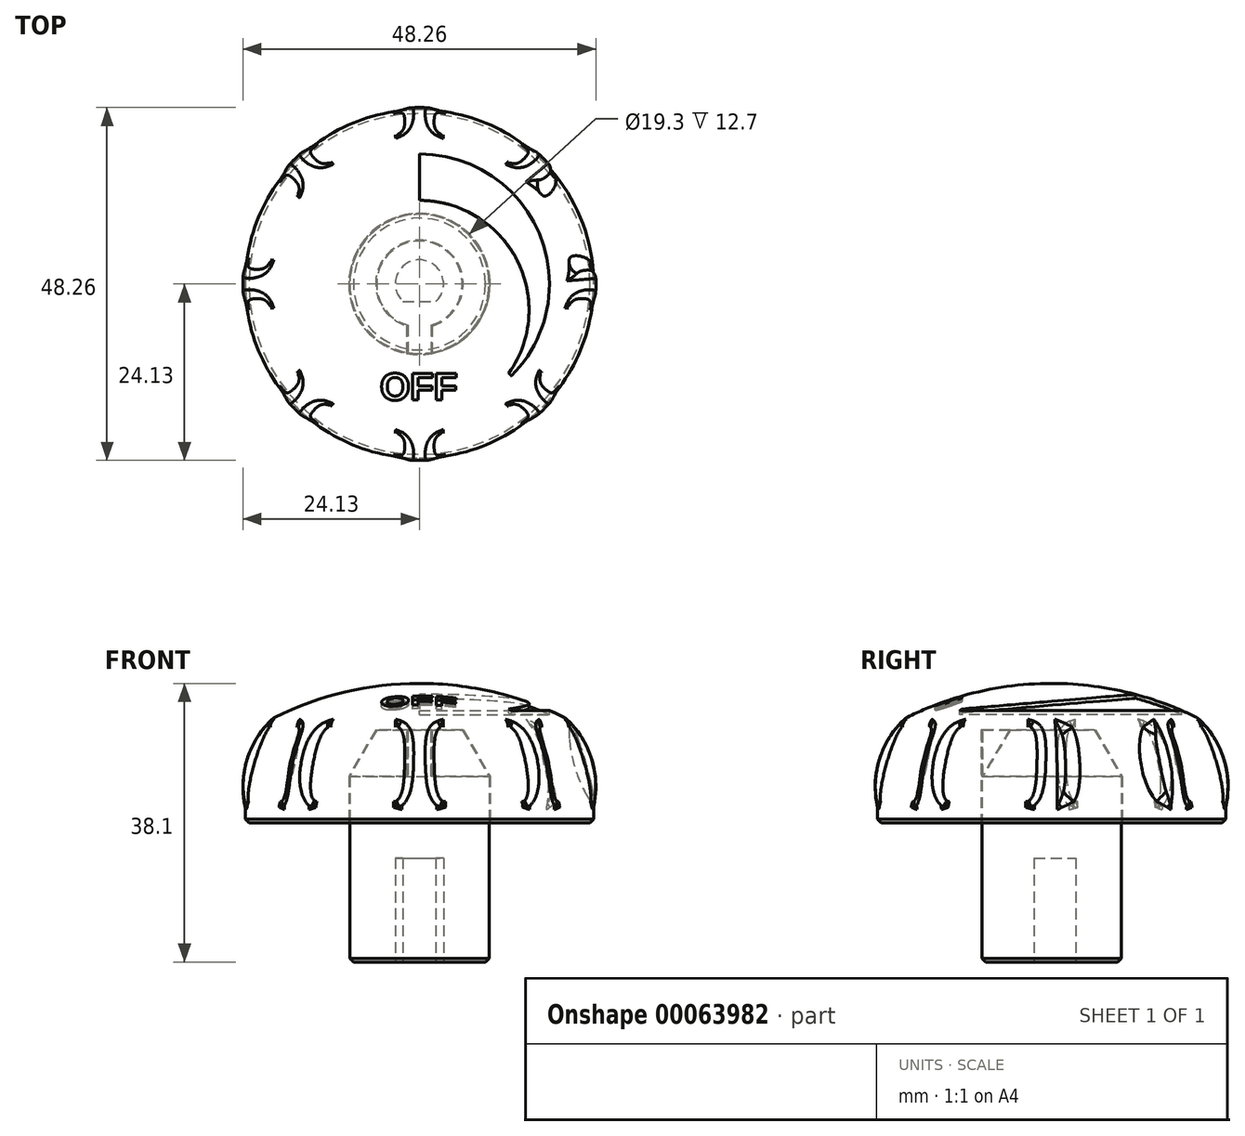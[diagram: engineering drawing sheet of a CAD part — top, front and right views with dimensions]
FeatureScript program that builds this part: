
annotation { "Feature Type Name" : "Feature", "Feature Type Description" : "" }
export const myFeature = defineFeature(function(context is Context, id is Id, definition is map)
    precondition{}
    {
        {
            var Q0;
            Q0=qCreatedBy(makeId("Front.planeOp"),FACE);
            var sketch = newSketch(context, id + "F0", { "sketchPlane" : qUnion([Q0])});
            skLineSegment(sketch, "E0", {"start": v(0, 0) * mm, "end": v(23.81, 0) * mm});
            skLineSegment(sketch, "E1", {"start": v(23.81, 0) * mm, "end": v(23.81, 2.54) * mm});
            skLineSegment(sketch, "E2", {"start": v(0, 0) * mm, "end": v(0, 19.05) * mm});
            skLineSegment(sketch, "E3.MirrorCS", {"start": v(-23.81, 0) * mm, "end": v(-23.81, 2.54) * mm, "construction": true});
            skLineSegment(sketch, "E4.MirrorCS", {"start": v(0, 0) * mm, "end": v(-23.81, 0) * mm, "construction": true});
            skArc(sketch, "E5", {"start": v(20.64, 13.97) * mm, "mid": v(0, 19.05) * mm, "end": v(-20.64, 13.97) * mm});
            skLineSegment(sketch, "E6", {"start": v(20.64, 13.97) * mm, "end": v(20.64, 0) * mm, "construction": true});
            skArc(sketch, "E7", {"start": v(20.64, 13.97) * mm, "mid": v(21.45, 8.04) * mm, "end": v(23.81, 2.54) * mm});
            skSolve(sketch);
        }
        {
            var Q0;
            Q0=makeQuery(id+"F0.imprint","IMPRINT",FACE,{"disambiguationData":[TD([[makeQuery(id+"F0.imprint","IMPRINT",EDGE,{"derivedFrom":sQuery(id+"F0.wireOp",EDGE,"E0")}),1.0]])]});
            var Q1;
            Q1=sQuery(id+"F0.wireOp",EDGE,"E2");
            revolve(context, id + "F1", {"entities" : qUnion([Q0]), "axis" : qUnion([Q1]), "revolveType" : RevolveType.FULL});
        }
        {
            var Q0;
            Q0=makeQuery(id+"F1.opRevolve","SWEPT_EDGE",EDGE,{"disambiguationData":[OSD([sQuery(id+"F0.wireOp",EDGE,"E1"),sQuery(id+"F0.wireOp",EDGE,"E7")])]});
            var Q1;
            Q1=makeQuery(id+"F1.opRevolve","SWEPT_EDGE",EDGE,{"disambiguationData":[OSD([sQuery(id+"F0.wireOp",EDGE,"E5"),sQuery(id+"F0.wireOp",EDGE,"E7")])]});
            fillet(context, id + "F2", {"entities" : qUnion([Q0, Q1]), "radius" : 1.59 * mm, "tangentPropagation" : true, "allowEdgeOverflow" : false});
        }
        {
            var Q0;
            Q0=qCreatedBy(makeId("Front.planeOp"),FACE);
            var sketch = newSketch(context, id + "F3", { "sketchPlane" : qUnion([Q0])});
            skLineSegment(sketch, "E8", {"start": v(0, 0) * mm, "end": v(0, 22.32) * mm, "construction": true});
            skLineSegment(sketch, "E9.0", {"start": v(23.81, 2.1) * mm, "end": v(-23.81, 2.1) * mm, "construction": true});
            skLineSegment(sketch, "E10.0", {"start": v(20.66, 13.05) * mm, "end": v(-20.66, 13.05) * mm, "construction": true});
            skArc(sketch, "E11", {"start": v(20.66, 13.05) * mm, "mid": v(20.4, 13.85) * mm, "end": v(19.78, 14.4) * mm});
            skArc(sketch, "E12", {"start": v(23.81, 2.1) * mm, "mid": v(23.76, 2.52) * mm, "end": v(23.6, 2.9) * mm});
            skArc(sketch, "E13", {"start": v(20.66, 13.05) * mm, "mid": v(21.51, 7.8) * mm, "end": v(23.6, 2.9) * mm});
            skLineSegment(sketch, "E14.0", {"start": v(-19.78, 14.4) * mm, "end": v(19.78, 14.4) * mm, "construction": true});
            skArc(sketch, "E15", {"start": v(23.81, 2.1) * mm, "mid": v(23.58, 8.6) * mm, "end": v(20.16, 14.14) * mm});
            skSolve(sketch);
        }
        {
            var Q0;
            Q0=makeQuery(id+"F3.imprint","IMPRINT",FACE,{"disambiguationData":[TD([[makeQuery(id+"F3.imprint","IMPRINT",EDGE,{"derivedFrom":sQuery(id+"F3.wireOp",EDGE,"E12")}),-1.0]])]});
            var Q1;
            Q1=sQuery(id+"F3.wireOp",EDGE,"E8");
            revolve(context, id + "F4", {"entities" : qUnion([Q0]), "axis" : qUnion([Q1]), "revolveType" : RevolveType.SYMMETRIC, "angle" : 10 * degree});
        }
        {
            var Q0;
            Q0=makeQuery(id+"F4.opRevolve","SWEPT_BODY",BODY,{"disambiguationData":[OSD([sQuery(id+"F3.wireOp",EDGE,"E11"),sQuery(id+"F3.wireOp",EDGE,"E12"),sQuery(id+"F3.wireOp",EDGE,"E13"),sQuery(id+"F3.wireOp",EDGE,"E15")])]});
            var Q1;
            Q1=makeQuery(id+"F1.opRevolve","SWEPT_EDGE",EDGE,{"disambiguationData":[OSD([sQuery(id+"F0.wireOp",EDGE,"E0"),sQuery(id+"F0.wireOp",EDGE,"E1")])]});
            circularPattern(context, id + "F5", {"entities" : qUnion([Q0]), "axis" : qUnion([Q1]), "angle" : 360 * degree, "instanceCount" : 8, "equalSpace" : true});
        }
        {
            var Q0;
            Q0=makeQuery(id+"F5.opPattern","COPY",BODY,{"derivedFrom":makeQuery(id+"F4.opRevolve","SWEPT_BODY",BODY,{"disambiguationData":[OSD([sQuery(id+"F3.wireOp",EDGE,"E11"),sQuery(id+"F3.wireOp",EDGE,"E12"),sQuery(id+"F3.wireOp",EDGE,"E13"),sQuery(id+"F3.wireOp",EDGE,"E15")])]}),"instanceName":"4"});
            var Q1;
            Q1=makeQuery(id+"F1.opRevolve","SWEPT_BODY",BODY,{"disambiguationData":[OSD([sQuery(id+"F0.wireOp",EDGE,"E0"),sQuery(id+"F0.wireOp",EDGE,"E1"),sQuery(id+"F0.wireOp",EDGE,"E2"),sQuery(id+"F0.wireOp",EDGE,"E5"),sQuery(id+"F0.wireOp",EDGE,"E7")])]});
            var Q2;
            Q2=makeQuery(id+"F5.opPattern","COPY",BODY,{"derivedFrom":makeQuery(id+"F4.opRevolve","SWEPT_BODY",BODY,{"disambiguationData":[OSD([sQuery(id+"F3.wireOp",EDGE,"E11"),sQuery(id+"F3.wireOp",EDGE,"E12"),sQuery(id+"F3.wireOp",EDGE,"E13"),sQuery(id+"F3.wireOp",EDGE,"E15")])]}),"instanceName":"7"});
            var Q3;
            Q3=makeQuery(id+"F5.opPattern","COPY",BODY,{"derivedFrom":makeQuery(id+"F4.opRevolve","SWEPT_BODY",BODY,{"disambiguationData":[OSD([sQuery(id+"F3.wireOp",EDGE,"E11"),sQuery(id+"F3.wireOp",EDGE,"E12"),sQuery(id+"F3.wireOp",EDGE,"E13"),sQuery(id+"F3.wireOp",EDGE,"E15")])]}),"instanceName":"6"});
            var Q4;
            Q4=makeQuery(id+"F5.opPattern","COPY",BODY,{"derivedFrom":makeQuery(id+"F4.opRevolve","SWEPT_BODY",BODY,{"disambiguationData":[OSD([sQuery(id+"F3.wireOp",EDGE,"E11"),sQuery(id+"F3.wireOp",EDGE,"E12"),sQuery(id+"F3.wireOp",EDGE,"E13"),sQuery(id+"F3.wireOp",EDGE,"E15")])]}),"instanceName":"5"});
            var Q5;
            Q5=makeQuery(id+"F4.opRevolve","SWEPT_BODY",BODY,{"disambiguationData":[OSD([sQuery(id+"F3.wireOp",EDGE,"E11"),sQuery(id+"F3.wireOp",EDGE,"E12"),sQuery(id+"F3.wireOp",EDGE,"E13"),sQuery(id+"F3.wireOp",EDGE,"E15")])]});
            var Q6;
            Q6=makeQuery(id+"F5.opPattern","COPY",BODY,{"derivedFrom":makeQuery(id+"F4.opRevolve","SWEPT_BODY",BODY,{"disambiguationData":[OSD([sQuery(id+"F3.wireOp",EDGE,"E11"),sQuery(id+"F3.wireOp",EDGE,"E12"),sQuery(id+"F3.wireOp",EDGE,"E13"),sQuery(id+"F3.wireOp",EDGE,"E15")])]}),"instanceName":"1"});
            var Q7;
            Q7=makeQuery(id+"F5.opPattern","COPY",BODY,{"derivedFrom":makeQuery(id+"F4.opRevolve","SWEPT_BODY",BODY,{"disambiguationData":[OSD([sQuery(id+"F3.wireOp",EDGE,"E11"),sQuery(id+"F3.wireOp",EDGE,"E12"),sQuery(id+"F3.wireOp",EDGE,"E13"),sQuery(id+"F3.wireOp",EDGE,"E15")])]}),"instanceName":"2"});
            var Q8;
            Q8=makeQuery(id+"F5.opPattern","COPY",BODY,{"derivedFrom":makeQuery(id+"F4.opRevolve","SWEPT_BODY",BODY,{"disambiguationData":[OSD([sQuery(id+"F3.wireOp",EDGE,"E11"),sQuery(id+"F3.wireOp",EDGE,"E12"),sQuery(id+"F3.wireOp",EDGE,"E13"),sQuery(id+"F3.wireOp",EDGE,"E15")])]}),"instanceName":"3"});
            booleanBodies(context, id + "F6", {"operationType" : BooleanOperationType.UNION, "tools" : qUnion([Q0, Q1, Q2, Q3, Q4, Q5, Q6, Q7, Q8])});
        }
        {
            var Q0;
            Q0=makeQuery(id+"F5.opPattern","COPY",EDGE,{"derivedFrom":makeQuery(id+"F4.opRevolve","CAP_EDGE",EDGE,{"disambiguationData":[OSD([sQuery(id+"F3.wireOp",EDGE,"E13")])],"isStart":false}),"instanceName":"4"});
            var Q1;
            Q1=makeQuery(id+"F5.opPattern","COPY",EDGE,{"derivedFrom":makeQuery(id+"F4.opRevolve","CAP_EDGE",EDGE,{"disambiguationData":[OSD([sQuery(id+"F3.wireOp",EDGE,"E13")])],"isStart":true}),"instanceName":"4"});
            var Q2;
            Q2=makeQuery(id+"F5.opPattern","COPY",EDGE,{"derivedFrom":makeQuery(id+"F4.opRevolve","CAP_EDGE",EDGE,{"disambiguationData":[OSD([sQuery(id+"F3.wireOp",EDGE,"E13")])],"isStart":false}),"instanceName":"5"});
            var Q3;
            Q3=makeQuery(id+"F5.opPattern","COPY",EDGE,{"derivedFrom":makeQuery(id+"F4.opRevolve","CAP_EDGE",EDGE,{"disambiguationData":[OSD([sQuery(id+"F3.wireOp",EDGE,"E13")])],"isStart":true}),"instanceName":"5"});
            var Q4;
            Q4=makeQuery(id+"F5.opPattern","COPY",EDGE,{"derivedFrom":makeQuery(id+"F4.opRevolve","CAP_EDGE",EDGE,{"disambiguationData":[OSD([sQuery(id+"F3.wireOp",EDGE,"E13")])],"isStart":false}),"instanceName":"6"});
            var Q5;
            Q5=makeQuery(id+"F5.opPattern","COPY",EDGE,{"derivedFrom":makeQuery(id+"F4.opRevolve","CAP_EDGE",EDGE,{"disambiguationData":[OSD([sQuery(id+"F3.wireOp",EDGE,"E13")])],"isStart":true}),"instanceName":"6"});
            var Q6;
            Q6=makeQuery(id+"F5.opPattern","COPY",EDGE,{"derivedFrom":makeQuery(id+"F4.opRevolve","CAP_EDGE",EDGE,{"disambiguationData":[OSD([sQuery(id+"F3.wireOp",EDGE,"E13")])],"isStart":false}),"instanceName":"7"});
            var Q7;
            Q7=makeQuery(id+"F5.opPattern","COPY",EDGE,{"derivedFrom":makeQuery(id+"F4.opRevolve","CAP_EDGE",EDGE,{"disambiguationData":[OSD([sQuery(id+"F3.wireOp",EDGE,"E13")])],"isStart":true}),"instanceName":"7"});
            var Q8;
            Q8=makeQuery(id+"F4.opRevolve","CAP_EDGE",EDGE,{"disambiguationData":[OSD([sQuery(id+"F3.wireOp",EDGE,"E13")])],"isStart":false});
            var Q9;
            Q9=makeQuery(id+"F4.opRevolve","CAP_EDGE",EDGE,{"disambiguationData":[OSD([sQuery(id+"F3.wireOp",EDGE,"E13")])],"isStart":true});
            var Q10;
            Q10=makeQuery(id+"F5.opPattern","COPY",EDGE,{"derivedFrom":makeQuery(id+"F4.opRevolve","CAP_EDGE",EDGE,{"disambiguationData":[OSD([sQuery(id+"F3.wireOp",EDGE,"E13")])],"isStart":false}),"instanceName":"1"});
            var Q11;
            Q11=makeQuery(id+"F5.opPattern","COPY",EDGE,{"derivedFrom":makeQuery(id+"F4.opRevolve","CAP_EDGE",EDGE,{"disambiguationData":[OSD([sQuery(id+"F3.wireOp",EDGE,"E13")])],"isStart":true}),"instanceName":"1"});
            var Q12;
            Q12=makeQuery(id+"F5.opPattern","COPY",EDGE,{"derivedFrom":makeQuery(id+"F4.opRevolve","CAP_EDGE",EDGE,{"disambiguationData":[OSD([sQuery(id+"F3.wireOp",EDGE,"E13")])],"isStart":false}),"instanceName":"2"});
            var Q13;
            Q13=makeQuery(id+"F5.opPattern","COPY",EDGE,{"derivedFrom":makeQuery(id+"F4.opRevolve","CAP_EDGE",EDGE,{"disambiguationData":[OSD([sQuery(id+"F3.wireOp",EDGE,"E13")])],"isStart":true}),"instanceName":"2"});
            var Q14;
            Q14=makeQuery(id+"F5.opPattern","COPY",EDGE,{"derivedFrom":makeQuery(id+"F4.opRevolve","CAP_EDGE",EDGE,{"disambiguationData":[OSD([sQuery(id+"F3.wireOp",EDGE,"E13")])],"isStart":false}),"instanceName":"3"});
            var Q15;
            Q15=makeQuery(id+"F5.opPattern","COPY",EDGE,{"derivedFrom":makeQuery(id+"F4.opRevolve","CAP_EDGE",EDGE,{"disambiguationData":[OSD([sQuery(id+"F3.wireOp",EDGE,"E13")])],"isStart":true}),"instanceName":"3"});
            fillet(context, id + "F7", {"entities" : qUnion([Q0, Q1, Q2, Q3, Q4, Q5, Q6, Q7, Q8, Q9, Q10, Q11, Q12, Q13, Q14, Q15]), "radius" : 1.59 * mm, "tangentPropagation" : true, "allowEdgeOverflow" : false});
        }
        {
            var Q0;
            Q0=makeQuery(id+"F5.opPattern","COPY",EDGE,{"derivedFrom":makeQuery(id+"F4.opRevolve","CAP_EDGE",EDGE,{"disambiguationData":[OSD([sQuery(id+"F3.wireOp",EDGE,"E15")])],"isStart":false}),"instanceName":"5"});
            var Q1;
            Q1=makeQuery(id+"F5.opPattern","COPY",EDGE,{"derivedFrom":makeQuery(id+"F4.opRevolve","CAP_EDGE",EDGE,{"disambiguationData":[OSD([sQuery(id+"F3.wireOp",EDGE,"E15")])],"isStart":true}),"instanceName":"5"});
            var Q2;
            Q2=makeQuery(id+"F5.opPattern","COPY",EDGE,{"derivedFrom":makeQuery(id+"F4.opRevolve","CAP_EDGE",EDGE,{"disambiguationData":[OSD([sQuery(id+"F3.wireOp",EDGE,"E15")])],"isStart":false}),"instanceName":"6"});
            var Q3;
            Q3=makeQuery(id+"F5.opPattern","COPY",EDGE,{"derivedFrom":makeQuery(id+"F4.opRevolve","CAP_EDGE",EDGE,{"disambiguationData":[OSD([sQuery(id+"F3.wireOp",EDGE,"E15")])],"isStart":true}),"instanceName":"6"});
            var Q4;
            Q4=makeQuery(id+"F5.opPattern","COPY",EDGE,{"derivedFrom":makeQuery(id+"F4.opRevolve","CAP_EDGE",EDGE,{"disambiguationData":[OSD([sQuery(id+"F3.wireOp",EDGE,"E15")])],"isStart":false}),"instanceName":"7"});
            var Q5;
            Q5=makeQuery(id+"F5.opPattern","COPY",EDGE,{"derivedFrom":makeQuery(id+"F4.opRevolve","CAP_EDGE",EDGE,{"disambiguationData":[OSD([sQuery(id+"F3.wireOp",EDGE,"E15")])],"isStart":true}),"instanceName":"7"});
            var Q6;
            Q6=makeQuery(id+"F4.opRevolve","CAP_EDGE",EDGE,{"disambiguationData":[OSD([sQuery(id+"F3.wireOp",EDGE,"E15")])],"isStart":false});
            var Q7;
            Q7=makeQuery(id+"F4.opRevolve","CAP_EDGE",EDGE,{"disambiguationData":[OSD([sQuery(id+"F3.wireOp",EDGE,"E15")])],"isStart":true});
            var Q8;
            Q8=makeQuery(id+"F5.opPattern","COPY",EDGE,{"derivedFrom":makeQuery(id+"F4.opRevolve","CAP_EDGE",EDGE,{"disambiguationData":[OSD([sQuery(id+"F3.wireOp",EDGE,"E15")])],"isStart":false}),"instanceName":"1"});
            var Q9;
            Q9=makeQuery(id+"F5.opPattern","COPY",EDGE,{"derivedFrom":makeQuery(id+"F4.opRevolve","CAP_EDGE",EDGE,{"disambiguationData":[OSD([sQuery(id+"F3.wireOp",EDGE,"E15")])],"isStart":true}),"instanceName":"1"});
            var Q10;
            Q10=makeQuery(id+"F5.opPattern","COPY",EDGE,{"derivedFrom":makeQuery(id+"F4.opRevolve","CAP_EDGE",EDGE,{"disambiguationData":[OSD([sQuery(id+"F3.wireOp",EDGE,"E15")])],"isStart":false}),"instanceName":"2"});
            var Q11;
            Q11=makeQuery(id+"F5.opPattern","COPY",EDGE,{"derivedFrom":makeQuery(id+"F4.opRevolve","CAP_EDGE",EDGE,{"disambiguationData":[OSD([sQuery(id+"F3.wireOp",EDGE,"E15")])],"isStart":true}),"instanceName":"2"});
            var Q12;
            Q12=makeQuery(id+"F5.opPattern","COPY",EDGE,{"derivedFrom":makeQuery(id+"F4.opRevolve","CAP_EDGE",EDGE,{"disambiguationData":[OSD([sQuery(id+"F3.wireOp",EDGE,"E15")])],"isStart":false}),"instanceName":"3"});
            var Q13;
            Q13=makeQuery(id+"F5.opPattern","COPY",EDGE,{"derivedFrom":makeQuery(id+"F4.opRevolve","CAP_EDGE",EDGE,{"disambiguationData":[OSD([sQuery(id+"F3.wireOp",EDGE,"E15")])],"isStart":true}),"instanceName":"3"});
            var Q14;
            Q14=makeQuery(id+"F5.opPattern","COPY",EDGE,{"derivedFrom":makeQuery(id+"F4.opRevolve","CAP_EDGE",EDGE,{"disambiguationData":[OSD([sQuery(id+"F3.wireOp",EDGE,"E15")])],"isStart":false}),"instanceName":"4"});
            var Q15;
            Q15=makeQuery(id+"F5.opPattern","COPY",EDGE,{"derivedFrom":makeQuery(id+"F4.opRevolve","CAP_EDGE",EDGE,{"disambiguationData":[OSD([sQuery(id+"F3.wireOp",EDGE,"E15")])],"isStart":true}),"instanceName":"4"});
            fillet(context, id + "F8", {"entities" : qUnion([Q0, Q1, Q2, Q3, Q4, Q5, Q6, Q7, Q8, Q9, Q10, Q11, Q12, Q13, Q14, Q15]), "radius" : 1.27 * mm, "tangentPropagation" : true, "allowEdgeOverflow" : false});
        }
        {
            var Q0;
            {var subQ0=sQuery(id+"F3.wireOp",EDGE,"E15");var subQ3=sQuery(id+"F3.wireOp",EDGE,"E13");var subQ4=sQuery(id+"F3.wireOp",EDGE,"E12");var subQ5=sQuery(id+"F3.wireOp",EDGE,"E11");var subQ6=makeQuery(id+"F4.opRevolve","CAP_FACE",FACE,{"disambiguationData":[OSD([subQ5,subQ4,subQ3,subQ0])],"isStart":true});var subQ7=sQuery(id+"F0.wireOp",EDGE,"E7");var subQ8=sQuery(id+"F0.wireOp",EDGE,"E1");var subQ10=makeQuery(id+"F1.opRevolve","SWEPT_FACE",FACE,{"disambiguationData":[OSD([subQ8])]});var subQ12=makeQuery(id+"F2.opFillet","BLEND_EDGE",EDGE,{"blendedFrom":[makeQuery(id+"F1.opRevolve","SWEPT_EDGE",EDGE,{"disambiguationData":[OSD([subQ8,subQ7])]}),subQ10],"blendedInto":[subQ10]});Q0=makeQuery(id+"F7.opFillet","MERGE",EDGE,{"derivedFrom":[makeQuery(id+"F6.opBoolean","MERGE",EDGE,{"derivedFrom":[subQ12,makeQuery(id+"F5.opPattern","COPY",EDGE,{"derivedFrom":makeQuery(id+"F4.opRevolve","SWEPT_EDGE",EDGE,{"disambiguationData":[OSD([subQ4,subQ0])]}),"instanceName":"6"})]}),makeQuery(id+"F6.opBoolean","SPLIT",EDGE,{"disambiguationData":[TD([makeQuery(id+"F5.opPattern","COPY",FACE,{"derivedFrom":subQ6,"instanceName":"5"})])],"derivedFrom":subQ12}),makeQuery(id+"F6.opBoolean","SPLIT",EDGE,{"disambiguationData":[TD([makeQuery(id+"F5.opPattern","COPY",FACE,{"derivedFrom":subQ6,"instanceName":"6"})])],"derivedFrom":subQ12})]});}
            var Q1;
            {var subQ0=sQuery(id+"F3.wireOp",EDGE,"E15");var subQ3=sQuery(id+"F3.wireOp",EDGE,"E13");var subQ4=sQuery(id+"F3.wireOp",EDGE,"E12");var subQ5=sQuery(id+"F3.wireOp",EDGE,"E11");var subQ6=makeQuery(id+"F4.opRevolve","CAP_FACE",FACE,{"disambiguationData":[OSD([subQ5,subQ4,subQ3,subQ0])],"isStart":true});var subQ7=sQuery(id+"F0.wireOp",EDGE,"E1");var subQ8=makeQuery(id+"F1.opRevolve","SWEPT_FACE",FACE,{"disambiguationData":[OSD([subQ7])]});var subQ9=sQuery(id+"F0.wireOp",EDGE,"E7");var subQ12=makeQuery(id+"F2.opFillet","BLEND_EDGE",EDGE,{"blendedFrom":[makeQuery(id+"F1.opRevolve","SWEPT_EDGE",EDGE,{"disambiguationData":[OSD([subQ7,subQ9])]}),subQ8],"blendedInto":[subQ8]});Q1=makeQuery(id+"F7.opFillet","MERGE",EDGE,{"derivedFrom":[makeQuery(id+"F6.opBoolean","MERGE",EDGE,{"derivedFrom":[subQ12,makeQuery(id+"F5.opPattern","COPY",EDGE,{"derivedFrom":makeQuery(id+"F4.opRevolve","SWEPT_EDGE",EDGE,{"disambiguationData":[OSD([subQ4,subQ0])]}),"instanceName":"5"})]}),makeQuery(id+"F6.opBoolean","SPLIT",EDGE,{"disambiguationData":[TD([makeQuery(id+"F5.opPattern","COPY",FACE,{"derivedFrom":subQ6,"instanceName":"4"})])],"derivedFrom":subQ12}),makeQuery(id+"F6.opBoolean","SPLIT",EDGE,{"disambiguationData":[TD([makeQuery(id+"F5.opPattern","COPY",FACE,{"derivedFrom":subQ6,"instanceName":"5"})])],"derivedFrom":subQ12})]});}
            var Q2;
            {var subQ0=sQuery(id+"F3.wireOp",EDGE,"E15");var subQ3=sQuery(id+"F3.wireOp",EDGE,"E13");var subQ4=sQuery(id+"F3.wireOp",EDGE,"E12");var subQ5=sQuery(id+"F3.wireOp",EDGE,"E11");var subQ6=makeQuery(id+"F4.opRevolve","CAP_FACE",FACE,{"disambiguationData":[OSD([subQ5,subQ4,subQ3,subQ0])],"isStart":true});var subQ7=sQuery(id+"F0.wireOp",EDGE,"E7");var subQ8=sQuery(id+"F0.wireOp",EDGE,"E1");var subQ10=makeQuery(id+"F1.opRevolve","SWEPT_FACE",FACE,{"disambiguationData":[OSD([subQ8])]});var subQ12=makeQuery(id+"F2.opFillet","BLEND_EDGE",EDGE,{"blendedFrom":[makeQuery(id+"F1.opRevolve","SWEPT_EDGE",EDGE,{"disambiguationData":[OSD([subQ8,subQ7])]}),subQ10],"blendedInto":[subQ10]});Q2=makeQuery(id+"F7.opFillet","MERGE",EDGE,{"derivedFrom":[makeQuery(id+"F6.opBoolean","MERGE",EDGE,{"derivedFrom":[subQ12,makeQuery(id+"F5.opPattern","COPY",EDGE,{"derivedFrom":makeQuery(id+"F4.opRevolve","SWEPT_EDGE",EDGE,{"disambiguationData":[OSD([subQ4,subQ0])]}),"instanceName":"4"})]}),makeQuery(id+"F6.opBoolean","SPLIT",EDGE,{"disambiguationData":[TD([makeQuery(id+"F5.opPattern","COPY",FACE,{"derivedFrom":subQ6,"instanceName":"3"})])],"derivedFrom":subQ12}),makeQuery(id+"F6.opBoolean","SPLIT",EDGE,{"disambiguationData":[TD([makeQuery(id+"F5.opPattern","COPY",FACE,{"derivedFrom":subQ6,"instanceName":"4"})])],"derivedFrom":subQ12})]});}
            var Q3;
            {var subQ0=sQuery(id+"F3.wireOp",EDGE,"E15");var subQ3=sQuery(id+"F0.wireOp",EDGE,"E7");var subQ4=sQuery(id+"F0.wireOp",EDGE,"E1");var subQ6=sQuery(id+"F3.wireOp",EDGE,"E13");var subQ7=sQuery(id+"F3.wireOp",EDGE,"E12");var subQ8=sQuery(id+"F3.wireOp",EDGE,"E11");var subQ9=makeQuery(id+"F4.opRevolve","CAP_FACE",FACE,{"disambiguationData":[OSD([subQ8,subQ7,subQ6,subQ0])],"isStart":true});var subQ10=makeQuery(id+"F1.opRevolve","SWEPT_FACE",FACE,{"disambiguationData":[OSD([subQ4])]});var subQ12=makeQuery(id+"F2.opFillet","BLEND_EDGE",EDGE,{"blendedFrom":[makeQuery(id+"F1.opRevolve","SWEPT_EDGE",EDGE,{"disambiguationData":[OSD([subQ4,subQ3])]}),subQ10],"blendedInto":[subQ10]});Q3=makeQuery(id+"F7.opFillet","MERGE",EDGE,{"derivedFrom":[makeQuery(id+"F6.opBoolean","MERGE",EDGE,{"derivedFrom":[subQ12,makeQuery(id+"F5.opPattern","COPY",EDGE,{"derivedFrom":makeQuery(id+"F4.opRevolve","SWEPT_EDGE",EDGE,{"disambiguationData":[OSD([subQ7,subQ0])]}),"instanceName":"3"})]}),makeQuery(id+"F6.opBoolean","SPLIT",EDGE,{"disambiguationData":[TD([makeQuery(id+"F5.opPattern","COPY",FACE,{"derivedFrom":subQ9,"instanceName":"2"})])],"derivedFrom":subQ12}),makeQuery(id+"F6.opBoolean","SPLIT",EDGE,{"disambiguationData":[TD([makeQuery(id+"F5.opPattern","COPY",FACE,{"derivedFrom":subQ9,"instanceName":"3"})])],"derivedFrom":subQ12})]});}
            var Q4;
            {var subQ0=sQuery(id+"F3.wireOp",EDGE,"E15");var subQ1=sQuery(id+"F3.wireOp",EDGE,"E13");var subQ2=sQuery(id+"F3.wireOp",EDGE,"E12");var subQ3=sQuery(id+"F3.wireOp",EDGE,"E11");var subQ4=makeQuery(id+"F4.opRevolve","CAP_FACE",FACE,{"disambiguationData":[OSD([subQ3,subQ2,subQ1,subQ0])],"isStart":true});var subQ7=sQuery(id+"F0.wireOp",EDGE,"E7");var subQ8=sQuery(id+"F0.wireOp",EDGE,"E1");var subQ10=makeQuery(id+"F1.opRevolve","SWEPT_FACE",FACE,{"disambiguationData":[OSD([subQ8])]});var subQ12=makeQuery(id+"F2.opFillet","BLEND_EDGE",EDGE,{"blendedFrom":[makeQuery(id+"F1.opRevolve","SWEPT_EDGE",EDGE,{"disambiguationData":[OSD([subQ8,subQ7])]}),subQ10],"blendedInto":[subQ10]});Q4=makeQuery(id+"F7.opFillet","MERGE",EDGE,{"derivedFrom":[makeQuery(id+"F6.opBoolean","MERGE",EDGE,{"derivedFrom":[subQ12,makeQuery(id+"F5.opPattern","COPY",EDGE,{"derivedFrom":makeQuery(id+"F4.opRevolve","SWEPT_EDGE",EDGE,{"disambiguationData":[OSD([subQ2,subQ0])]}),"instanceName":"2"})]}),makeQuery(id+"F6.opBoolean","SPLIT",EDGE,{"disambiguationData":[TD([makeQuery(id+"F5.opPattern","COPY",FACE,{"derivedFrom":subQ4,"instanceName":"1"})])],"derivedFrom":subQ12}),makeQuery(id+"F6.opBoolean","SPLIT",EDGE,{"disambiguationData":[TD([makeQuery(id+"F5.opPattern","COPY",FACE,{"derivedFrom":subQ4,"instanceName":"2"})])],"derivedFrom":subQ12})]});}
            var Q5;
            {var subQ0=sQuery(id+"F3.wireOp",EDGE,"E15");var subQ3=sQuery(id+"F3.wireOp",EDGE,"E13");var subQ4=sQuery(id+"F3.wireOp",EDGE,"E12");var subQ5=sQuery(id+"F3.wireOp",EDGE,"E11");var subQ6=makeQuery(id+"F4.opRevolve","CAP_FACE",FACE,{"disambiguationData":[OSD([subQ5,subQ4,subQ3,subQ0])],"isStart":true});var subQ7=sQuery(id+"F0.wireOp",EDGE,"E7");var subQ8=sQuery(id+"F0.wireOp",EDGE,"E1");var subQ10=makeQuery(id+"F1.opRevolve","SWEPT_FACE",FACE,{"disambiguationData":[OSD([subQ8])]});var subQ12=makeQuery(id+"F2.opFillet","BLEND_EDGE",EDGE,{"blendedFrom":[makeQuery(id+"F1.opRevolve","SWEPT_EDGE",EDGE,{"disambiguationData":[OSD([subQ8,subQ7])]}),subQ10],"blendedInto":[subQ10]});Q5=makeQuery(id+"F7.opFillet","MERGE",EDGE,{"derivedFrom":[makeQuery(id+"F6.opBoolean","MERGE",EDGE,{"derivedFrom":[subQ12,makeQuery(id+"F5.opPattern","COPY",EDGE,{"derivedFrom":makeQuery(id+"F4.opRevolve","SWEPT_EDGE",EDGE,{"disambiguationData":[OSD([subQ4,subQ0])]}),"instanceName":"1"})]}),makeQuery(id+"F6.opBoolean","SPLIT",EDGE,{"disambiguationData":[TD([subQ6])],"derivedFrom":subQ12}),makeQuery(id+"F6.opBoolean","SPLIT",EDGE,{"disambiguationData":[TD([makeQuery(id+"F5.opPattern","COPY",FACE,{"derivedFrom":subQ6,"instanceName":"1"})])],"derivedFrom":subQ12})]});}
            var Q6;
            {var subQ0=sQuery(id+"F3.wireOp",EDGE,"E15");var subQ2=sQuery(id+"F3.wireOp",EDGE,"E13");var subQ3=sQuery(id+"F3.wireOp",EDGE,"E12");var subQ4=sQuery(id+"F3.wireOp",EDGE,"E11");var subQ5=makeQuery(id+"F4.opRevolve","CAP_FACE",FACE,{"disambiguationData":[OSD([subQ4,subQ3,subQ2,subQ0])],"isStart":false});var subQ6=sQuery(id+"F0.wireOp",EDGE,"E7");var subQ7=sQuery(id+"F0.wireOp",EDGE,"E1");var subQ9=makeQuery(id+"F1.opRevolve","SWEPT_FACE",FACE,{"disambiguationData":[OSD([subQ7])]});var subQ10=makeQuery(id+"F4.opRevolve","CAP_FACE",FACE,{"disambiguationData":[OSD([subQ4,subQ3,subQ2,subQ0])],"isStart":true});var subQ11=makeQuery(id+"F2.opFillet","BLEND_EDGE",EDGE,{"blendedFrom":[makeQuery(id+"F1.opRevolve","SWEPT_EDGE",EDGE,{"disambiguationData":[OSD([subQ7,subQ6])]}),subQ9],"blendedInto":[subQ9]});Q6=makeQuery(id+"F7.opFillet","MERGE",EDGE,{"derivedFrom":[makeQuery(id+"F6.opBoolean","MERGE",EDGE,{"derivedFrom":[subQ11,makeQuery(id+"F4.opRevolve","SWEPT_EDGE",EDGE,{"disambiguationData":[OSD([subQ3,subQ0])]})]}),makeQuery(id+"F6.opBoolean","SPLIT",EDGE,{"disambiguationData":[TD([subQ10])],"derivedFrom":subQ11}),makeQuery(id+"F6.opBoolean","SPLIT",EDGE,{"disambiguationData":[TD([subQ5])],"derivedFrom":subQ11})]});}
            var Q7;
            {var subQ0=sQuery(id+"F3.wireOp",EDGE,"E15");var subQ2=sQuery(id+"F3.wireOp",EDGE,"E13");var subQ3=sQuery(id+"F3.wireOp",EDGE,"E12");var subQ4=sQuery(id+"F3.wireOp",EDGE,"E11");var subQ5=makeQuery(id+"F4.opRevolve","CAP_FACE",FACE,{"disambiguationData":[OSD([subQ4,subQ3,subQ2,subQ0])],"isStart":true});var subQ6=sQuery(id+"F0.wireOp",EDGE,"E7");var subQ7=sQuery(id+"F0.wireOp",EDGE,"E1");var subQ9=makeQuery(id+"F1.opRevolve","SWEPT_FACE",FACE,{"disambiguationData":[OSD([subQ7])]});var subQ10=makeQuery(id+"F4.opRevolve","CAP_FACE",FACE,{"disambiguationData":[OSD([subQ4,subQ3,subQ2,subQ0])],"isStart":false});var subQ12=makeQuery(id+"F2.opFillet","BLEND_EDGE",EDGE,{"blendedFrom":[makeQuery(id+"F1.opRevolve","SWEPT_EDGE",EDGE,{"disambiguationData":[OSD([subQ7,subQ6])]}),subQ9],"blendedInto":[subQ9]});Q7=makeQuery(id+"F7.opFillet","MERGE",EDGE,{"derivedFrom":[makeQuery(id+"F6.opBoolean","MERGE",EDGE,{"derivedFrom":[subQ12,makeQuery(id+"F5.opPattern","COPY",EDGE,{"derivedFrom":makeQuery(id+"F4.opRevolve","SWEPT_EDGE",EDGE,{"disambiguationData":[OSD([subQ3,subQ0])]}),"instanceName":"7"})]}),makeQuery(id+"F6.opBoolean","SPLIT",EDGE,{"disambiguationData":[TD([subQ10])],"derivedFrom":subQ12}),makeQuery(id+"F6.opBoolean","SPLIT",EDGE,{"disambiguationData":[TD([makeQuery(id+"F5.opPattern","COPY",FACE,{"derivedFrom":subQ5,"instanceName":"6"})])],"derivedFrom":subQ12})]});}
            fillet(context, id + "F9", {"entities" : qUnion([Q0, Q1, Q2, Q3, Q4, Q5, Q6, Q7]), "radius" : 2.54 * mm, "tangentPropagation" : true, "allowEdgeOverflow" : false});
        }
        {
            var Q0;
            Q0=qCreatedBy(makeId("Front.planeOp"),FACE);
            var sketch = newSketch(context, id + "F10", { "sketchPlane" : qUnion([Q0])});
            skLineSegment(sketch, "E16.0.0", {"start": v(23.55, 0) * mm, "end": v(-22.88, 0) * mm, "construction": true});
            skArc(sketch, "E17", {"start": v(19.78, 14.4) * mm, "mid": v(0, 19.05) * mm, "end": v(-19.78, 14.4) * mm, "construction": true});
            skLineSegment(sketch, "E18", {"start": v(0, 0) * mm, "end": v(0, 19.05) * mm, "construction": true});
            skLineSegment(sketch, "E19", {"start": v(0, 0) * mm, "end": v(0, -25.4) * mm, "construction": true});
            skLineSegment(sketch, "E20", {"start": v(0, 12.7) * mm, "end": v(5.99, 12.7) * mm});
            skLineSegment(sketch, "E21", {"start": v(5.99, 12.7) * mm, "end": v(9.65, 6.35) * mm});
            skLineSegment(sketch, "E22", {"start": v(9.65, 6.35) * mm, "end": v(9.65, 0) * mm});
            skLineSegment(sketch, "E23", {"start": v(9.65, 0) * mm, "end": v(0, 0) * mm});
            skLineSegment(sketch, "E24", {"start": v(0, 12.7) * mm, "end": v(0, 0) * mm});
            skSolve(sketch);
        }
        {
            var Q0;
            Q0 = qSketchRegion(id + "F10", true);
            var Q1;
            Q1=sQuery(id+"F10.wireOp",EDGE,"E19");
            revolve(context, id + "F11", {"operationType" : NewBodyOperationType.REMOVE, "entities" : qUnion([Q0]), "axis" : qUnion([Q1]), "revolveType" : RevolveType.FULL, "oppositeDirection" : true});
        }
        {
            var Q0;
            Q0=makeQuery(id+"F11.boolean.opBoolean","COPY",FACE,{"derivedFrom":makeQuery(id+"F11.opRevolve","SWEPT_FACE",FACE,{"disambiguationData":[OSD([sQuery(id+"F10.wireOp",EDGE,"E20")])]})});
            var sketch = newSketch(context, id + "F12", { "sketchPlane" : qUnion([Q0])});
            skArc(sketch, "E25.0", {"start": v(1.71, 9.5) * mm, "mid": v(0, 9.65) * mm, "end": v(-1.71, 9.5) * mm});
            skLineSegment(sketch, "E26", {"start": v(0, 0) * mm, "end": v(0, 9.65) * mm, "construction": true});
            skLineSegment(sketch, "E27", {"start": v(1.71, 9.5) * mm, "end": v(1.71, 5.74) * mm});
            skLineSegment(sketch, "E28", {"start": v(-1.71, 9.5) * mm, "end": v(-1.71, 5.74) * mm});
            skLineSegment(sketch, "E29", {"start": v(1.71, 5.74) * mm, "end": v(-1.71, 5.74) * mm});
            skSolve(sketch);
        }
        {
            var Q0;
            Q0 = qSketchRegion(id + "F12", true);
            var Q1;
            Q1=makeQuery(id+"F1.opRevolve","SWEPT_FACE",FACE,{"disambiguationData":[OSD([sQuery(id+"F0.wireOp",EDGE,"E0")])]});
            extrude(context, id + "F13", {"entities" : qUnion([Q0]), "operationType" : NewBodyOperationType.REMOVE, "endBound" : BoundingType.UP_TO_SURFACE, "endBoundEntityFace" : qUnion([Q1]), "depth" : 25.4 * mm});
        }
        {
            var Q0;
            Q0=qCreatedBy(makeId("Front.planeOp"),FACE);
            var sketch = newSketch(context, id + "F14", { "sketchPlane" : qUnion([Q0])});
            skLineSegment(sketch, "E30", {"start": v(0, 0) * mm, "end": v(0, 26.18) * mm, "construction": true});
            skLineSegment(sketch, "E31", {"start": v(0, 12.7) * mm, "end": v(5.86, 12.7) * mm});
            skLineSegment(sketch, "E32", {"start": v(5.86, 12.7) * mm, "end": v(9.53, 6.35) * mm});
            skLineSegment(sketch, "E33", {"start": v(9.53, 6.35) * mm, "end": v(9.53, -19.05) * mm});
            skLineSegment(sketch, "E34", {"start": v(0, 12.7) * mm, "end": v(0, -19.05) * mm});
            skLineSegment(sketch, "E35", {"start": v(0, -19.05) * mm, "end": v(9.53, -19.05) * mm});
            skSolve(sketch);
        }
        {
            var Q0;
            Q0 = qSketchRegion(id + "F14", true);
            var Q1;
            Q1=sQuery(id+"F14.wireOp",EDGE,"E30");
            revolve(context, id + "F15", {"entities" : qUnion([Q0]), "axis" : qUnion([Q1]), "revolveType" : RevolveType.FULL});
        }
        {
            var Q0;
            Q0=makeQuery(id+"F15.opRevolve","SWEPT_FACE",FACE,{"disambiguationData":[OSD([sQuery(id+"F14.wireOp",EDGE,"E31")])]});
            var sketch = newSketch(context, id + "F16", { "sketchPlane" : qUnion([Q0])});
            skArc(sketch, "E36.0", {"start": v(-1.59, -9.4) * mm, "mid": v(0, -9.53) * mm, "end": v(1.59, -9.4) * mm});
            skLineSegment(sketch, "E37", {"start": v(0, 0) * mm, "end": v(0, -9.53) * mm, "construction": true});
            skLineSegment(sketch, "E38", {"start": v(-1.59, -5.64) * mm, "end": v(-1.59, -9.4) * mm});
            skLineSegment(sketch, "E39", {"start": v(1.59, -5.64) * mm, "end": v(1.59, -9.4) * mm});
            skLineSegment(sketch, "E40", {"start": v(1.59, -5.64) * mm, "end": v(-1.59, -5.64) * mm, "construction": true});
            skSolve(sketch);
        }
        {
            var Q0;
            Q0=makeQuery(id+"F16.imprint","IMPRINT",FACE,{"disambiguationData":[TD([[makeQuery(id+"F16.imprint","IMPRINT",EDGE,{"derivedFrom":sQuery(id+"F16.wireOp",EDGE,"E36.0")}),1.0]])]});
            var Q1;
            Q1=makeQuery(id+"F15.opRevolve","SWEPT_FACE",FACE,{"disambiguationData":[OSD([sQuery(id+"F14.wireOp",EDGE,"E32")])]});
            extrude(context, id + "F17", {"entities" : qUnion([Q0]), "operationType" : NewBodyOperationType.ADD, "endBound" : BoundingType.UP_TO_SURFACE, "oppositeDirection" : true, "endBoundEntityFace" : qUnion([Q1]), "depth" : 25.4 * mm});
        }
        {
            var Q0;
            Q0=makeQuery(id+"F15.opRevolve","SWEPT_FACE",FACE,{"disambiguationData":[OSD([sQuery(id+"F14.wireOp",EDGE,"E35")])]});
            var sketch = newSketch(context, id + "F18", { "sketchPlane" : qUnion([Q0])});
            skArc(sketch, "E41", {"start": v(-2.25, 2.41) * mm, "mid": v(0, -3.3) * mm, "end": v(2.25, 2.41) * mm});
            skLineSegment(sketch, "E42", {"start": v(-2.25, 2.41) * mm, "end": v(2.25, 2.41) * mm});
            skLineSegment(sketch, "E43", {"start": v(0, 2.41) * mm, "end": v(0, -3.3) * mm, "construction": true});
            skSolve(sketch);
        }
        {
            var Q0;
            Q0=makeQuery(id+"F18.imprint","IMPRINT",FACE,{"disambiguationData":[TD([[makeQuery(id+"F18.imprint","IMPRINT",EDGE,{"derivedFrom":sQuery(id+"F18.wireOp",EDGE,"E41")}),1.0]])]});
            extrude(context, id + "F19", {"entities" : qUnion([Q0]), "operationType" : NewBodyOperationType.REMOVE, "oppositeDirection" : true, "depth" : 14.22 * mm});
        }
        {
            var Q0;
            Q0=makeQuery(id+"F1.opRevolve","SWEPT_EDGE",EDGE,{"disambiguationData":[OSD([sQuery(id+"F0.wireOp",EDGE,"E0"),sQuery(id+"F0.wireOp",EDGE,"E1")])]});
            var Q1;
            Q1=makeQuery(id+"F11.boolean.opBoolean","COPY",EDGE,{"derivedFrom":makeQuery(id+"F11.opRevolve","SWEPT_EDGE",EDGE,{"disambiguationData":[OSD([sQuery(id+"F10.wireOp",EDGE,"E22"),sQuery(id+"F10.wireOp",EDGE,"E23")])]})});
            chamfer(context, id + "F20", {"entities" : qUnion([Q0, Q1]), "width" : 0.5 * mm, "tangentPropagation" : true});
        }
        {
            var Q0;
            Q0=makeQuery(id+"F15.opRevolve","SWEPT_EDGE",EDGE,{"disambiguationData":[OSD([sQuery(id+"F14.wireOp",EDGE,"E33"),sQuery(id+"F14.wireOp",EDGE,"E35")])]});
            var Q1;
            Q1=makeQuery(id+"F19.boolean.opBoolean","COPY",EDGE,{"derivedFrom":makeQuery(id+"F19.opExtrude","CAP_EDGE",EDGE,{"disambiguationData":[OSD([sQuery(id+"F18.wireOp",EDGE,"E42")])],"isStart":true})});
            var Q2;
            Q2=makeQuery(id+"F19.boolean.opBoolean","COPY",EDGE,{"derivedFrom":makeQuery(id+"F19.opExtrude","CAP_EDGE",EDGE,{"disambiguationData":[OSD([sQuery(id+"F18.wireOp",EDGE,"E41")])],"isStart":true})});
            var Q3;
            Q3=makeQuery(id+"F17.opExtrude","CAP_EDGE",EDGE,{"disambiguationData":[OSD([sQuery(id+"F16.wireOp",EDGE,"E39")])],"isStart":true});
            var Q4;
            Q4=makeQuery(id+"F17.opExtrude","CAP_EDGE",EDGE,{"disambiguationData":[OSD([sQuery(id+"F16.wireOp",EDGE,"E36.0")])],"isStart":true});
            var Q5;
            Q5=makeQuery(id+"F17.opExtrude","CAP_EDGE",EDGE,{"disambiguationData":[OSD([sQuery(id+"F16.wireOp",EDGE,"E38")])],"isStart":true});
            var Q6;
            Q6=makeQuery(id+"F15.opRevolve","SWEPT_EDGE",EDGE,{"disambiguationData":[OSD([sQuery(id+"F14.wireOp",EDGE,"E31"),sQuery(id+"F14.wireOp",EDGE,"E32")])]});
            chamfer(context, id + "F21", {"entities" : qUnion([Q0, Q1, Q2, Q3, Q4, Q5, Q6]), "width" : 0.5 * mm, "tangentPropagation" : true});
        }
        {
            var Q0;
            Q0=qCreatedBy(makeId("Top.planeOp"),FACE);
            cPlane(context, id + "F22", {"entities" : qUnion([Q0]), "cplaneType" : CPlaneType.OFFSET, "offset" : 20.32 * mm, "width" : 152.4 * mm, "height" : 152.4 * mm});
        }
        {
            var Q0;
            Q0=qCreatedBy(id+"F22.planeOp",FACE);
            var sketch = newSketch(context, id + "F23", { "sketchPlane" : qUnion([Q0])});
            skLineSegment(sketch, "E44", {"start": v(0, 0) * mm, "end": v(0, -12.06) * mm, "construction": true});
            skText(sketch, "E45", { "text": "OFF", "fontName": "Arimo-Bold.ttf"});
            const initialGuessF23  = {"E45": [-0.00538, -0.01588, 1, 0, 0.00381]};
            skSetInitialGuess(sketch, initialGuessF23);
            skSolve(sketch);
        }
        {
            var Q0;
            Q0=qCreatedBy(id+"F22.planeOp",FACE);
            var sketch = newSketch(context, id + "F24", { "sketchPlane" : qUnion([Q0])});
            skArc(sketch, "E46", {"start": v(12.57, -12.57) * mm, "mid": v(16.43, 6.8) * mm, "end": v(0, 17.78) * mm});
            skLineSegment(sketch, "E47", {"start": v(0, 17.78) * mm, "end": v(0, 0) * mm, "construction": true});
            skLineSegment(sketch, "E48", {"start": v(0, 0) * mm, "end": v(12.57, -12.57) * mm, "construction": true});
            skLineSegment(sketch, "E49", {"start": v(0, 17.78) * mm, "end": v(0, 11.43) * mm});
            skLineSegment(sketch, "E50", {"start": v(0, 11.43) * mm, "end": v(13.62, 11.43) * mm, "construction": true});
            skLineSegment(sketch, "E51", {"start": v(12.57, -12.57) * mm, "end": v(12.22, -12.22) * mm});
            skArc(sketch, "E52", {"start": v(12.22, -12.22) * mm, "mid": v(13.3, 3.33) * mm, "end": v(0, 11.43) * mm});
            skSolve(sketch);
        }
        {
            var Q0;
            Q0 = qSketchRegion(id + "F23", true);
            var Q1;
            Q1 = qSketchRegion(id + "F24", true);
            var Q2;
            Q2=makeQuery(id+"F1.opRevolve","SWEPT_FACE",FACE,{"disambiguationData":[OSD([sQuery(id+"F0.wireOp",EDGE,"E0")])]});
            extrude(context, id + "F25", {"entities" : qUnion([Q0, Q1]), "endBound" : BoundingType.UP_TO_SURFACE, "oppositeDirection" : true, "endBoundEntityFace" : qUnion([Q2]), "depth" : 25.4 * mm});
        }
        {
            var Q0;
            Q0=qCreatedBy(makeId("Front.planeOp"),FACE);
            var sketch = newSketch(context, id + "F26", { "sketchPlane" : qUnion([Q0])});
            skArc(sketch, "E53", {"start": v(19.83, 14.38) * mm, "mid": v(0, 19.05) * mm, "end": v(-19.83, 14.38) * mm, "construction": true});
            skArc(sketch, "E54.0", {"start": v(20, 14.72) * mm, "mid": v(0, 19.43) * mm, "end": v(-20, 14.72) * mm});
            skArc(sketch, "E55.0", {"start": v(19.6, 13.93) * mm, "mid": v(0, 18.54) * mm, "end": v(-19.6, 13.93) * mm});
            skLineSegment(sketch, "E56", {"start": v(-20, 14.72) * mm, "end": v(-19.6, 13.93) * mm, "construction": true});
            skLineSegment(sketch, "E57", {"start": v(19.6, 13.93) * mm, "end": v(20, 14.72) * mm});
            skLineSegment(sketch, "E58", {"start": v(0, 0) * mm, "end": v(0, 19.43) * mm, "construction": true});
            skLineSegment(sketch, "E59", {"start": v(0, -25.4) * mm, "end": v(19.6, 13.93) * mm, "construction": true});
            skLineSegment(sketch, "E60", {"start": v(0, -25.4) * mm, "end": v(-19.6, 13.93) * mm, "construction": true});
            skLineSegment(sketch, "E61", {"start": v(0, 19.43) * mm, "end": v(0, 18.54) * mm});
            skSolve(sketch);
        }
        {
            var Q0;
            Q0 = qSketchRegion(id + "F26", true);
            var Q1;
            Q1=sQuery(id+"F26.wireOp",EDGE,"E58");
            revolve(context, id + "F27", {"entities" : qUnion([Q0]), "axis" : qUnion([Q1]), "revolveType" : RevolveType.FULL});
        }
        {
            var Q0;
            Q0=makeQuery(id+"F27.opRevolve","SWEPT_BODY",BODY,{"disambiguationData":[OSD([sQuery(id+"F26.wireOp",EDGE,"E54.0"),sQuery(id+"F26.wireOp",EDGE,"E55.0"),sQuery(id+"F26.wireOp",EDGE,"E57"),sQuery(id+"F26.wireOp",EDGE,"E61")])]});
            var Q1;
            Q1=makeQuery(id+"F25.opExtrude","SWEPT_BODY",BODY,{"disambiguationData":[OSD([sQuery(id+"F23.wireOp",EDGE,"E45.sketch_text.stroke-0"),sQuery(id+"F23.wireOp",EDGE,"E45.sketch_text.stroke-1"),sQuery(id+"F23.wireOp",EDGE,"E45.sketch_text.stroke-2"),sQuery(id+"F23.wireOp",EDGE,"E45.sketch_text.stroke-3"),sQuery(id+"F23.wireOp",EDGE,"E45.sketch_text.stroke-4"),sQuery(id+"F23.wireOp",EDGE,"E45.sketch_text.stroke-5"),sQuery(id+"F23.wireOp",EDGE,"E45.sketch_text.stroke-6"),sQuery(id+"F23.wireOp",EDGE,"E45.sketch_text.stroke-7"),sQuery(id+"F23.wireOp",EDGE,"E45.sketch_text.stroke-8"),sQuery(id+"F23.wireOp",EDGE,"E45.sketch_text.stroke-9"),sQuery(id+"F23.wireOp",EDGE,"E45.sketch_text.stroke-10"),sQuery(id+"F23.wireOp",EDGE,"E45.sketch_text.stroke-11"),sQuery(id+"F23.wireOp",EDGE,"E45.sketch_text.stroke-12"),sQuery(id+"F23.wireOp",EDGE,"E45.sketch_text.stroke-13"),sQuery(id+"F23.wireOp",EDGE,"E45.sketch_text.stroke-14"),sQuery(id+"F23.wireOp",EDGE,"E45.sketch_text.stroke-15"),sQuery(id+"F23.wireOp",EDGE,"E45.sketch_text.stroke-16")])]});
            booleanBodies(context, id + "F28", {"operationType" : BooleanOperationType.INTERSECTION, "tools" : qUnion([Q0, Q1]), "keepTools" : true});
        }
        {
            var Q0;
            Q0=makeQuery(id+"F27.opRevolve","SWEPT_BODY",BODY,{"disambiguationData":[OSD([sQuery(id+"F26.wireOp",EDGE,"E54.0"),sQuery(id+"F26.wireOp",EDGE,"E55.0"),sQuery(id+"F26.wireOp",EDGE,"E57"),sQuery(id+"F26.wireOp",EDGE,"E61")])]});
            var Q1;
            Q1=makeQuery(id+"F25.opExtrude","SWEPT_BODY",BODY,{"disambiguationData":[OSD([sQuery(id+"F23.wireOp",EDGE,"E45.sketch_text.stroke-17"),sQuery(id+"F23.wireOp",EDGE,"E45.sketch_text.stroke-18"),sQuery(id+"F23.wireOp",EDGE,"E45.sketch_text.stroke-19"),sQuery(id+"F23.wireOp",EDGE,"E45.sketch_text.stroke-20"),sQuery(id+"F23.wireOp",EDGE,"E45.sketch_text.stroke-21"),sQuery(id+"F23.wireOp",EDGE,"E45.sketch_text.stroke-22"),sQuery(id+"F23.wireOp",EDGE,"E45.sketch_text.stroke-23"),sQuery(id+"F23.wireOp",EDGE,"E45.sketch_text.stroke-24"),sQuery(id+"F23.wireOp",EDGE,"E45.sketch_text.stroke-25"),sQuery(id+"F23.wireOp",EDGE,"E45.sketch_text.stroke-26")])]});
            booleanBodies(context, id + "F29", {"operationType" : BooleanOperationType.INTERSECTION, "tools" : qUnion([Q0, Q1]), "keepTools" : true});
        }
        {
            var Q0;
            Q0=makeQuery(id+"F25.opExtrude","SWEPT_BODY",BODY,{"disambiguationData":[OSD([sQuery(id+"F23.wireOp",EDGE,"E45.sketch_text.stroke-27"),sQuery(id+"F23.wireOp",EDGE,"E45.sketch_text.stroke-28"),sQuery(id+"F23.wireOp",EDGE,"E45.sketch_text.stroke-29"),sQuery(id+"F23.wireOp",EDGE,"E45.sketch_text.stroke-30"),sQuery(id+"F23.wireOp",EDGE,"E45.sketch_text.stroke-31"),sQuery(id+"F23.wireOp",EDGE,"E45.sketch_text.stroke-32"),sQuery(id+"F23.wireOp",EDGE,"E45.sketch_text.stroke-33"),sQuery(id+"F23.wireOp",EDGE,"E45.sketch_text.stroke-34"),sQuery(id+"F23.wireOp",EDGE,"E45.sketch_text.stroke-35"),sQuery(id+"F23.wireOp",EDGE,"E45.sketch_text.stroke-36")])]});
            var Q1;
            Q1=makeQuery(id+"F27.opRevolve","SWEPT_BODY",BODY,{"disambiguationData":[OSD([sQuery(id+"F26.wireOp",EDGE,"E54.0"),sQuery(id+"F26.wireOp",EDGE,"E55.0"),sQuery(id+"F26.wireOp",EDGE,"E57"),sQuery(id+"F26.wireOp",EDGE,"E61")])]});
            booleanBodies(context, id + "F30", {"operationType" : BooleanOperationType.INTERSECTION, "tools" : qUnion([Q0, Q1]), "keepTools" : true});
        }
        {
            var Q0;
            Q0=makeQuery(id+"F25.opExtrude","SWEPT_BODY",BODY,{"disambiguationData":[OSD([sQuery(id+"F24.wireOp",EDGE,"E46"),sQuery(id+"F24.wireOp",EDGE,"E49"),sQuery(id+"F24.wireOp",EDGE,"E51"),sQuery(id+"F24.wireOp",EDGE,"E52")])]});
            var Q1;
            Q1=makeQuery(id+"F27.opRevolve","SWEPT_BODY",BODY,{"disambiguationData":[OSD([sQuery(id+"F26.wireOp",EDGE,"E54.0"),sQuery(id+"F26.wireOp",EDGE,"E55.0"),sQuery(id+"F26.wireOp",EDGE,"E57"),sQuery(id+"F26.wireOp",EDGE,"E61")])]});
            booleanBodies(context, id + "F31", {"operationType" : BooleanOperationType.INTERSECTION, "tools" : qUnion([Q0, Q1]), "keepTools" : true});
        }
        {
            var Q0;
            Q0=makeQuery(id+"F25.opExtrude","SWEPT_BODY",BODY,{"disambiguationData":[OSD([sQuery(id+"F24.wireOp",EDGE,"E46"),sQuery(id+"F24.wireOp",EDGE,"E49"),sQuery(id+"F24.wireOp",EDGE,"E51"),sQuery(id+"F24.wireOp",EDGE,"E52")])]});
            var Q1;
            Q1=makeQuery(id+"F25.opExtrude","SWEPT_BODY",BODY,{"disambiguationData":[OSD([sQuery(id+"F23.wireOp",EDGE,"E45.sketch_text.stroke-27"),sQuery(id+"F23.wireOp",EDGE,"E45.sketch_text.stroke-28"),sQuery(id+"F23.wireOp",EDGE,"E45.sketch_text.stroke-29"),sQuery(id+"F23.wireOp",EDGE,"E45.sketch_text.stroke-30"),sQuery(id+"F23.wireOp",EDGE,"E45.sketch_text.stroke-31"),sQuery(id+"F23.wireOp",EDGE,"E45.sketch_text.stroke-32"),sQuery(id+"F23.wireOp",EDGE,"E45.sketch_text.stroke-33"),sQuery(id+"F23.wireOp",EDGE,"E45.sketch_text.stroke-34"),sQuery(id+"F23.wireOp",EDGE,"E45.sketch_text.stroke-35"),sQuery(id+"F23.wireOp",EDGE,"E45.sketch_text.stroke-36")])]});
            var Q2;
            Q2=makeQuery(id+"F25.opExtrude","SWEPT_BODY",BODY,{"disambiguationData":[OSD([sQuery(id+"F23.wireOp",EDGE,"E45.sketch_text.stroke-17"),sQuery(id+"F23.wireOp",EDGE,"E45.sketch_text.stroke-18"),sQuery(id+"F23.wireOp",EDGE,"E45.sketch_text.stroke-19"),sQuery(id+"F23.wireOp",EDGE,"E45.sketch_text.stroke-20"),sQuery(id+"F23.wireOp",EDGE,"E45.sketch_text.stroke-21"),sQuery(id+"F23.wireOp",EDGE,"E45.sketch_text.stroke-22"),sQuery(id+"F23.wireOp",EDGE,"E45.sketch_text.stroke-23"),sQuery(id+"F23.wireOp",EDGE,"E45.sketch_text.stroke-24"),sQuery(id+"F23.wireOp",EDGE,"E45.sketch_text.stroke-25"),sQuery(id+"F23.wireOp",EDGE,"E45.sketch_text.stroke-26")])]});
            var Q3;
            Q3=makeQuery(id+"F25.opExtrude","SWEPT_BODY",BODY,{"disambiguationData":[OSD([sQuery(id+"F23.wireOp",EDGE,"E45.sketch_text.stroke-0"),sQuery(id+"F23.wireOp",EDGE,"E45.sketch_text.stroke-1"),sQuery(id+"F23.wireOp",EDGE,"E45.sketch_text.stroke-2"),sQuery(id+"F23.wireOp",EDGE,"E45.sketch_text.stroke-3"),sQuery(id+"F23.wireOp",EDGE,"E45.sketch_text.stroke-4"),sQuery(id+"F23.wireOp",EDGE,"E45.sketch_text.stroke-5"),sQuery(id+"F23.wireOp",EDGE,"E45.sketch_text.stroke-6"),sQuery(id+"F23.wireOp",EDGE,"E45.sketch_text.stroke-7"),sQuery(id+"F23.wireOp",EDGE,"E45.sketch_text.stroke-8"),sQuery(id+"F23.wireOp",EDGE,"E45.sketch_text.stroke-9"),sQuery(id+"F23.wireOp",EDGE,"E45.sketch_text.stroke-10"),sQuery(id+"F23.wireOp",EDGE,"E45.sketch_text.stroke-11"),sQuery(id+"F23.wireOp",EDGE,"E45.sketch_text.stroke-12"),sQuery(id+"F23.wireOp",EDGE,"E45.sketch_text.stroke-13"),sQuery(id+"F23.wireOp",EDGE,"E45.sketch_text.stroke-14"),sQuery(id+"F23.wireOp",EDGE,"E45.sketch_text.stroke-15"),sQuery(id+"F23.wireOp",EDGE,"E45.sketch_text.stroke-16")])]});
            var Q4;
            Q4=makeQuery(id+"F27.opRevolve","SWEPT_BODY",BODY,{"disambiguationData":[OSD([sQuery(id+"F26.wireOp",EDGE,"E54.0"),sQuery(id+"F26.wireOp",EDGE,"E55.0"),sQuery(id+"F26.wireOp",EDGE,"E57"),sQuery(id+"F26.wireOp",EDGE,"E61")])]});
            deleteBodies(context, id + "F32", {"entities" : qUnion([Q0, Q1, Q2, Q3, Q4])});
        }
        {
            var Q0;
            Q0=makeQuery(id+"F28.opBoolean","INTERSECT",BODY,{"derivedFrom":[makeQuery(id+"F25.opExtrude","SWEPT_BODY",BODY,{"disambiguationData":[OSD([sQuery(id+"F23.wireOp",EDGE,"E45.sketch_text.stroke-0"),sQuery(id+"F23.wireOp",EDGE,"E45.sketch_text.stroke-1"),sQuery(id+"F23.wireOp",EDGE,"E45.sketch_text.stroke-2"),sQuery(id+"F23.wireOp",EDGE,"E45.sketch_text.stroke-3"),sQuery(id+"F23.wireOp",EDGE,"E45.sketch_text.stroke-4"),sQuery(id+"F23.wireOp",EDGE,"E45.sketch_text.stroke-5"),sQuery(id+"F23.wireOp",EDGE,"E45.sketch_text.stroke-6"),sQuery(id+"F23.wireOp",EDGE,"E45.sketch_text.stroke-7"),sQuery(id+"F23.wireOp",EDGE,"E45.sketch_text.stroke-8"),sQuery(id+"F23.wireOp",EDGE,"E45.sketch_text.stroke-9"),sQuery(id+"F23.wireOp",EDGE,"E45.sketch_text.stroke-10"),sQuery(id+"F23.wireOp",EDGE,"E45.sketch_text.stroke-11"),sQuery(id+"F23.wireOp",EDGE,"E45.sketch_text.stroke-12"),sQuery(id+"F23.wireOp",EDGE,"E45.sketch_text.stroke-13"),sQuery(id+"F23.wireOp",EDGE,"E45.sketch_text.stroke-14"),sQuery(id+"F23.wireOp",EDGE,"E45.sketch_text.stroke-15"),sQuery(id+"F23.wireOp",EDGE,"E45.sketch_text.stroke-16")])]}),makeQuery(id+"F27.opRevolve","SWEPT_BODY",BODY,{"disambiguationData":[OSD([sQuery(id+"F26.wireOp",EDGE,"E54.0"),sQuery(id+"F26.wireOp",EDGE,"E55.0"),sQuery(id+"F26.wireOp",EDGE,"E57"),sQuery(id+"F26.wireOp",EDGE,"E61")])]})]});
            var Q1;
            Q1=makeQuery(id+"F29.opBoolean","INTERSECT",BODY,{"derivedFrom":[makeQuery(id+"F25.opExtrude","SWEPT_BODY",BODY,{"disambiguationData":[OSD([sQuery(id+"F23.wireOp",EDGE,"E45.sketch_text.stroke-17"),sQuery(id+"F23.wireOp",EDGE,"E45.sketch_text.stroke-18"),sQuery(id+"F23.wireOp",EDGE,"E45.sketch_text.stroke-19"),sQuery(id+"F23.wireOp",EDGE,"E45.sketch_text.stroke-20"),sQuery(id+"F23.wireOp",EDGE,"E45.sketch_text.stroke-21"),sQuery(id+"F23.wireOp",EDGE,"E45.sketch_text.stroke-22"),sQuery(id+"F23.wireOp",EDGE,"E45.sketch_text.stroke-23"),sQuery(id+"F23.wireOp",EDGE,"E45.sketch_text.stroke-24"),sQuery(id+"F23.wireOp",EDGE,"E45.sketch_text.stroke-25"),sQuery(id+"F23.wireOp",EDGE,"E45.sketch_text.stroke-26")])]}),makeQuery(id+"F27.opRevolve","SWEPT_BODY",BODY,{"disambiguationData":[OSD([sQuery(id+"F26.wireOp",EDGE,"E54.0"),sQuery(id+"F26.wireOp",EDGE,"E55.0"),sQuery(id+"F26.wireOp",EDGE,"E57"),sQuery(id+"F26.wireOp",EDGE,"E61")])]})]});
            var Q2;
            Q2=makeQuery(id+"F30.opBoolean","INTERSECT",BODY,{"derivedFrom":[makeQuery(id+"F25.opExtrude","SWEPT_BODY",BODY,{"disambiguationData":[OSD([sQuery(id+"F23.wireOp",EDGE,"E45.sketch_text.stroke-27"),sQuery(id+"F23.wireOp",EDGE,"E45.sketch_text.stroke-28"),sQuery(id+"F23.wireOp",EDGE,"E45.sketch_text.stroke-29"),sQuery(id+"F23.wireOp",EDGE,"E45.sketch_text.stroke-30"),sQuery(id+"F23.wireOp",EDGE,"E45.sketch_text.stroke-31"),sQuery(id+"F23.wireOp",EDGE,"E45.sketch_text.stroke-32"),sQuery(id+"F23.wireOp",EDGE,"E45.sketch_text.stroke-33"),sQuery(id+"F23.wireOp",EDGE,"E45.sketch_text.stroke-34"),sQuery(id+"F23.wireOp",EDGE,"E45.sketch_text.stroke-35"),sQuery(id+"F23.wireOp",EDGE,"E45.sketch_text.stroke-36")])]}),makeQuery(id+"F27.opRevolve","SWEPT_BODY",BODY,{"disambiguationData":[OSD([sQuery(id+"F26.wireOp",EDGE,"E54.0"),sQuery(id+"F26.wireOp",EDGE,"E55.0"),sQuery(id+"F26.wireOp",EDGE,"E57"),sQuery(id+"F26.wireOp",EDGE,"E61")])]})]});
            var Q3;
            Q3=makeQuery(id+"F31.opBoolean","INTERSECT",BODY,{"derivedFrom":[makeQuery(id+"F25.opExtrude","SWEPT_BODY",BODY,{"disambiguationData":[OSD([sQuery(id+"F24.wireOp",EDGE,"E46"),sQuery(id+"F24.wireOp",EDGE,"E49"),sQuery(id+"F24.wireOp",EDGE,"E51"),sQuery(id+"F24.wireOp",EDGE,"E52")])]}),makeQuery(id+"F27.opRevolve","SWEPT_BODY",BODY,{"disambiguationData":[OSD([sQuery(id+"F26.wireOp",EDGE,"E54.0"),sQuery(id+"F26.wireOp",EDGE,"E55.0"),sQuery(id+"F26.wireOp",EDGE,"E57"),sQuery(id+"F26.wireOp",EDGE,"E61")])]})]});
            var Q4;
            Q4=makeQuery(id+"F5.opPattern","COPY",BODY,{"derivedFrom":makeQuery(id+"F4.opRevolve","SWEPT_BODY",BODY,{"disambiguationData":[OSD([sQuery(id+"F3.wireOp",EDGE,"E11"),sQuery(id+"F3.wireOp",EDGE,"E12"),sQuery(id+"F3.wireOp",EDGE,"E13"),sQuery(id+"F3.wireOp",EDGE,"E15")])]}),"instanceName":"4"});
            booleanBodies(context, id + "F33", {"operationType" : BooleanOperationType.SUBTRACTION, "tools" : qUnion([Q0, Q1, Q2, Q3]), "targets" : qUnion([Q4])});
        }
    });
